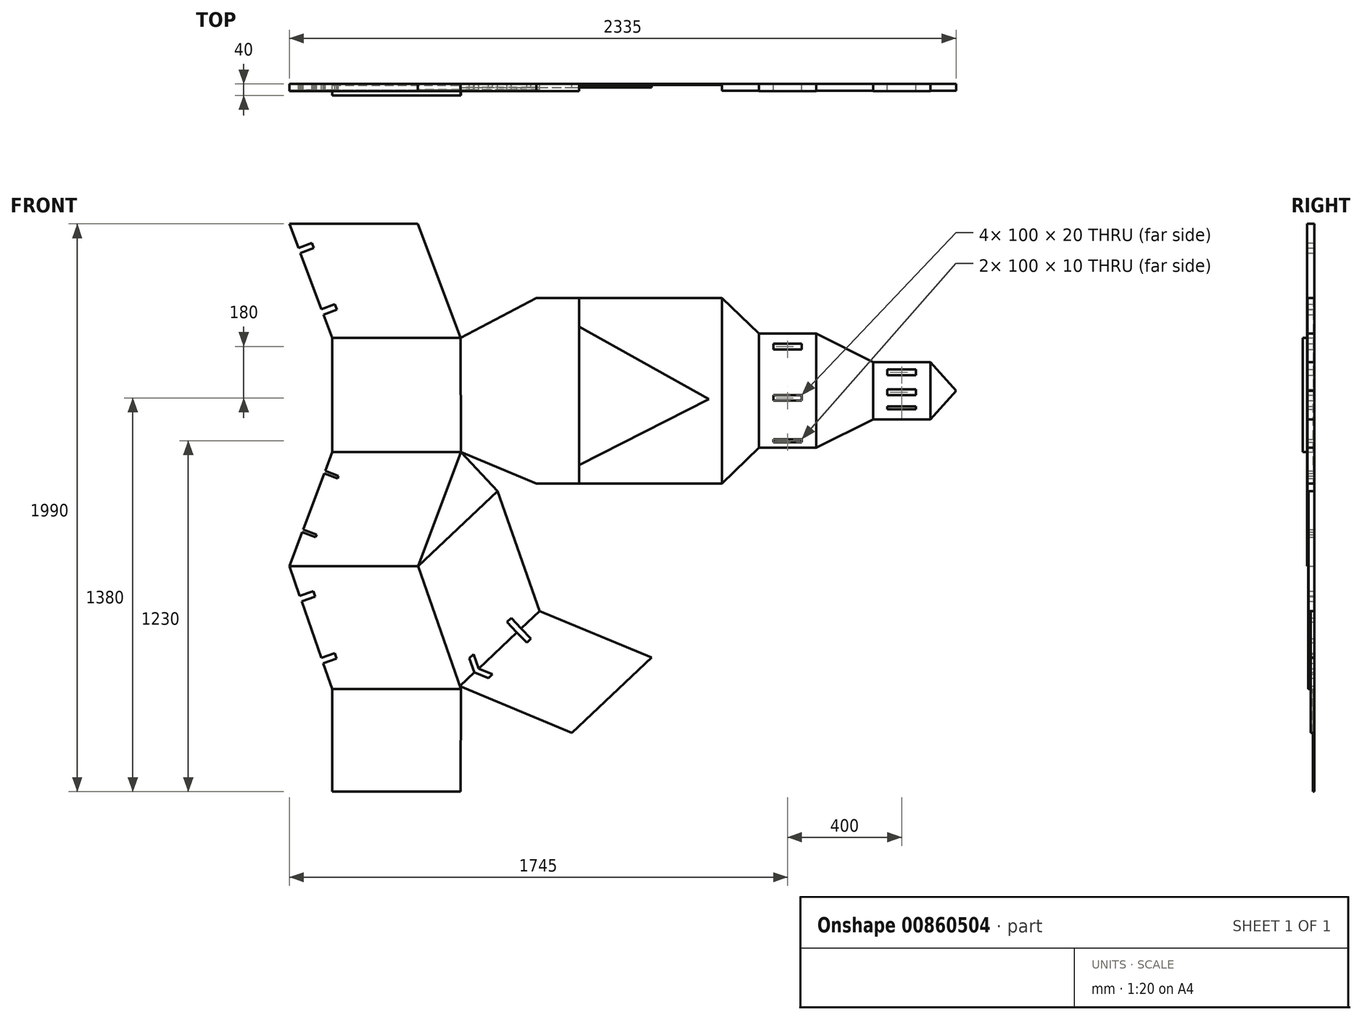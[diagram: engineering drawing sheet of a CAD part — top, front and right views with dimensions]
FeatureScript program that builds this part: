
annotation { "Feature Type Name" : "Feature", "Feature Type Description" : "" }
export const myFeature = defineFeature(function(context is Context, id is Id, definition is map)
    precondition{}
    {
        {
            var Q0;
            Q0=qCreatedBy(makeId("Front.planeOp"),FACE);
            var sketch = newSketch(context, id + "F0", { "sketchPlane" : qUnion([Q0])});
            skLineSegment(sketch, "E0", {"start": v(-600.47, 910) * mm, "end": v(-150.47, 910) * mm});
            skLineSegment(sketch, "E1", {"start": v(-150.47, 910) * mm, "end": v(-0.47, 510) * mm});
            skLineSegment(sketch, "E2", {"start": v(-0.47, 510) * mm, "end": v(-450.47, 510) * mm});
            skLineSegment(sketch, "E3", {"start": v(-450.47, 510) * mm, "end": v(-481.09, 591.65) * mm});
            skLineSegment(sketch, "E4", {"start": v(-450.47, 510) * mm, "end": v(-450.47, 110) * mm});
            skLineSegment(sketch, "E5", {"start": v(-450.47, 110) * mm, "end": v(0, 110) * mm});
            skLineSegment(sketch, "E6", {"start": v(0, 110) * mm, "end": v(-0.47, 510) * mm});
            skLineSegment(sketch, "E7", {"start": v(-450.47, 110) * mm, "end": v(-475.05, 44.46) * mm});
            skLineSegment(sketch, "E8", {"start": v(-600.47, -290) * mm, "end": v(-150, -290) * mm});
            skLineSegment(sketch, "E9", {"start": v(-150, -290) * mm, "end": v(0, 110) * mm});
            skLineSegment(sketch, "E10", {"start": v(-600.47, -290) * mm, "end": v(-564.24, -393.86) * mm});
            skLineSegment(sketch, "E11", {"start": v(-450.47, -720) * mm, "end": v(0, -720) * mm});
            skLineSegment(sketch, "E12", {"start": v(0, -720) * mm, "end": v(-150, -290) * mm});
            skLineSegment(sketch, "E13", {"start": v(-450.47, -720) * mm, "end": v(-450.47, -1080) * mm});
            skLineSegment(sketch, "E14", {"start": v(-450.47, -1080) * mm, "end": v(-0.47, -1080) * mm});
            skLineSegment(sketch, "E15", {"start": v(-0.47, -1080) * mm, "end": v(0, -720) * mm});
            skLineSegment(sketch, "E16", {"start": v(-0.47, 510) * mm, "end": v(264.53, 650) * mm});
            skLineSegment(sketch, "E17", {"start": v(264.53, 650) * mm, "end": v(414.53, 650) * mm});
            skLineSegment(sketch, "E18", {"start": v(414.53, 650) * mm, "end": v(414.53, 0) * mm});
            skLineSegment(sketch, "E19", {"start": v(414.53, 0) * mm, "end": v(264.53, 0) * mm});
            skLineSegment(sketch, "E20", {"start": v(264.53, 0) * mm, "end": v(0, 110) * mm});
            skLineSegment(sketch, "E21.bottom", {"start": v(414.53, 650) * mm, "end": v(914.53, 650) * mm});
            skLineSegment(sketch, "E21.top", {"start": v(414.53, 0) * mm, "end": v(914.53, 0) * mm});
            skLineSegment(sketch, "E21.right", {"start": v(914.53, 650) * mm, "end": v(914.53, 0) * mm});
            skPoint(sketch, "E22", {"position": v(414.53, 65) * mm});
            skPoint(sketch, "E23", {"position": v(414.53, 550) * mm});
            skPoint(sketch, "E24", {"position": v(869.53, 295) * mm});
            skLineSegment(sketch, "E25", {"start": v(414.53, 550) * mm, "end": v(869.53, 295) * mm});
            skLineSegment(sketch, "E26", {"start": v(414.53, 65) * mm, "end": v(869.53, 295) * mm});
            skLineSegment(sketch, "E27", {"start": v(914.53, 650) * mm, "end": v(1044.53, 525) * mm});
            skLineSegment(sketch, "E28", {"start": v(1044.53, 525) * mm, "end": v(1044.53, 125) * mm});
            skLineSegment(sketch, "E29", {"start": v(1044.53, 125) * mm, "end": v(914.53, 0) * mm});
            skLineSegment(sketch, "E30.bottom", {"start": v(1044.53, 525) * mm, "end": v(1244.53, 525) * mm});
            skLineSegment(sketch, "E30.top", {"start": v(1044.53, 125) * mm, "end": v(1244.53, 125) * mm});
            skLineSegment(sketch, "E30.right", {"start": v(1244.53, 525) * mm, "end": v(1244.53, 125) * mm});
            skLineSegment(sketch, "E31", {"start": v(1244.53, 525) * mm, "end": v(1444.53, 425) * mm});
            skLineSegment(sketch, "E32", {"start": v(1444.53, 425) * mm, "end": v(1444.53, 225) * mm});
            skLineSegment(sketch, "E33", {"start": v(1444.53, 225) * mm, "end": v(1244.53, 125) * mm});
            skLineSegment(sketch, "E34.bottom", {"start": v(1444.53, 425) * mm, "end": v(1644.53, 425) * mm});
            skLineSegment(sketch, "E34.top", {"start": v(1444.53, 225) * mm, "end": v(1644.53, 225) * mm});
            skLineSegment(sketch, "E34.right", {"start": v(1644.53, 425) * mm, "end": v(1644.53, 225) * mm});
            skLineSegment(sketch, "E35", {"start": v(1644.53, 225) * mm, "end": v(1734.53, 325) * mm});
            skLineSegment(sketch, "E36", {"start": v(1734.53, 325) * mm, "end": v(1644.53, 425) * mm});
            skLineSegment(sketch, "E37", {"start": v(-150, -290) * mm, "end": v(128.9, -26.38) * mm});
            skLineSegment(sketch, "E38", {"start": v(128.9, -26.38) * mm, "end": v(0, 110) * mm});
            skLineSegment(sketch, "E39", {"start": v(128.9, -26.38) * mm, "end": v(275.61, -446.93) * mm});
            skLineSegment(sketch, "E40", {"start": v(275.61, -446.93) * mm, "end": v(211.1, -507.92) * mm});
            skLineSegment(sketch, "E41", {"start": v(275.61, -446.93) * mm, "end": v(667.98, -610.25) * mm});
            skLineSegment(sketch, "E42", {"start": v(-3.3, -710.56) * mm, "end": v(389.07, -873.88) * mm});
            skLineSegment(sketch, "E43", {"start": v(389.07, -873.88) * mm, "end": v(667.98, -610.25) * mm});
            skLineSegment(sketch, "E44", {"start": v(-568.87, 825.73) * mm, "end": v(-522.05, 843.29) * mm});
            skLineSegment(sketch, "E45", {"start": v(-522.05, 843.29) * mm, "end": v(-515.03, 824.56) * mm});
            skLineSegment(sketch, "E46", {"start": v(-515.03, 824.56) * mm, "end": v(-561.84, 807) * mm});
            skLineSegment(sketch, "E47", {"start": v(-488.1, 610.37) * mm, "end": v(-441.3, 627.93) * mm});
            skLineSegment(sketch, "E48", {"start": v(-441.3, 627.93) * mm, "end": v(-434.27, 609.2) * mm});
            skLineSegment(sketch, "E49", {"start": v(-434.27, 609.2) * mm, "end": v(-481.09, 591.65) * mm});
            skLineSegment(sketch, "E50.trimOffspring", {"start": v(-568.87, 825.73) * mm, "end": v(-600.47, 910) * mm});
            skLineSegment(sketch, "E51.trimOffspring", {"start": v(-488.1, 610.37) * mm, "end": v(-561.84, 807) * mm});
            skLineSegment(sketch, "E52", {"start": v(-475.05, 44.46) * mm, "end": v(-428.23, 26.9) * mm});
            skLineSegment(sketch, "E53", {"start": v(-428.23, 26.9) * mm, "end": v(-431.74, 17.54) * mm});
            skLineSegment(sketch, "E54", {"start": v(-431.74, 17.54) * mm, "end": v(-478.56, 35.1) * mm});
            skLineSegment(sketch, "E55", {"start": v(-552.3, -161.54) * mm, "end": v(-505.48, -179.1) * mm});
            skLineSegment(sketch, "E56", {"start": v(-505.48, -179.1) * mm, "end": v(-508.99, -188.45) * mm});
            skLineSegment(sketch, "E57", {"start": v(-508.99, -188.45) * mm, "end": v(-555.8, -170.9) * mm});
            skLineSegment(sketch, "E58.trimOffspring", {"start": v(-478.56, 35.1) * mm, "end": v(-552.3, -161.54) * mm});
            skLineSegment(sketch, "E59.trimOffspring", {"start": v(-555.8, -170.9) * mm, "end": v(-600.47, -290) * mm});
            skLineSegment(sketch, "E60", {"start": v(-564.24, -393.86) * mm, "end": v(-517.03, -377.4) * mm});
            skLineSegment(sketch, "E61", {"start": v(-517.03, -377.4) * mm, "end": v(-510.44, -396.28) * mm});
            skLineSegment(sketch, "E62", {"start": v(-510.44, -396.28) * mm, "end": v(-557.65, -412.75) * mm});
            skLineSegment(sketch, "E63", {"start": v(-441.27, -594.56) * mm, "end": v(-441.27, -594.56) * mm});
            skLineSegment(sketch, "E64", {"start": v(-441.27, -594.56) * mm, "end": v(-488.48, -611.03) * mm});
            skLineSegment(sketch, "E65", {"start": v(-441.27, -594.56) * mm, "end": v(-434.68, -613.44) * mm});
            skLineSegment(sketch, "E66", {"start": v(-434.68, -613.44) * mm, "end": v(-481.9, -629.91) * mm});
            skLineSegment(sketch, "E67.trimOffspring", {"start": v(-557.65, -412.75) * mm, "end": v(-488.48, -611.03) * mm});
            skLineSegment(sketch, "E68.trimOffspring", {"start": v(-481.9, -629.91) * mm, "end": v(-450.47, -720) * mm});
            skLineSegment(sketch, "E69.bottom", {"start": v(1094.53, 490) * mm, "end": v(1194.53, 490) * mm});
            skLineSegment(sketch, "E69.top", {"start": v(1094.53, 470) * mm, "end": v(1194.53, 470) * mm});
            skLineSegment(sketch, "E69.left", {"start": v(1094.53, 490) * mm, "end": v(1094.53, 470) * mm});
            skLineSegment(sketch, "E69.right", {"start": v(1194.53, 490) * mm, "end": v(1194.53, 470) * mm});
            skLineSegment(sketch, "E70.bottom", {"start": v(1094.53, 310) * mm, "end": v(1194.53, 310) * mm});
            skLineSegment(sketch, "E70.top", {"start": v(1094.53, 290) * mm, "end": v(1194.53, 290) * mm});
            skLineSegment(sketch, "E70.left", {"start": v(1094.53, 310) * mm, "end": v(1094.53, 290) * mm});
            skLineSegment(sketch, "E70.right", {"start": v(1194.53, 310) * mm, "end": v(1194.53, 290) * mm});
            skLineSegment(sketch, "E71.bottom", {"start": v(1094.53, 155) * mm, "end": v(1194.53, 155) * mm});
            skLineSegment(sketch, "E71.top", {"start": v(1094.53, 145) * mm, "end": v(1194.53, 145) * mm});
            skLineSegment(sketch, "E71.left", {"start": v(1094.53, 155) * mm, "end": v(1094.53, 145) * mm});
            skLineSegment(sketch, "E71.right", {"start": v(1194.53, 155) * mm, "end": v(1194.53, 145) * mm});
            skLineSegment(sketch, "E72.bottom", {"start": v(1494.53, 400) * mm, "end": v(1594.53, 400) * mm});
            skLineSegment(sketch, "E72.top", {"start": v(1494.53, 380) * mm, "end": v(1594.53, 380) * mm});
            skLineSegment(sketch, "E72.left", {"start": v(1494.53, 400) * mm, "end": v(1494.53, 380) * mm});
            skLineSegment(sketch, "E72.right", {"start": v(1594.53, 400) * mm, "end": v(1594.53, 380) * mm});
            skLineSegment(sketch, "E73.bottom", {"start": v(1494.53, 330) * mm, "end": v(1594.53, 330) * mm});
            skLineSegment(sketch, "E73.top", {"start": v(1494.53, 310) * mm, "end": v(1594.53, 310) * mm});
            skLineSegment(sketch, "E73.left", {"start": v(1494.53, 330) * mm, "end": v(1494.53, 310) * mm});
            skLineSegment(sketch, "E73.right", {"start": v(1594.53, 330) * mm, "end": v(1594.53, 310) * mm});
            skLineSegment(sketch, "E74.bottom", {"start": v(1494.53, 270) * mm, "end": v(1594.53, 270) * mm});
            skLineSegment(sketch, "E74.top", {"start": v(1494.53, 260) * mm, "end": v(1594.53, 260) * mm});
            skLineSegment(sketch, "E74.left", {"start": v(1494.53, 270) * mm, "end": v(1494.53, 260) * mm});
            skLineSegment(sketch, "E74.right", {"start": v(1594.53, 270) * mm, "end": v(1594.53, 260) * mm});
            skPoint(sketch, "E75", {"position": v(47.58, -662.47) * mm});
            skPoint(sketch, "E76", {"position": v(62.11, -648.74) * mm});
            skPoint(sketch, "E77", {"position": v(196.56, -521.65) * mm});
            skPoint(sketch, "E78", {"position": v(211.1, -507.92) * mm});
            skLineSegment(sketch, "E79", {"start": v(47.58, -662.47) * mm, "end": v(30.14, -612.47) * mm});
            skLineSegment(sketch, "E80", {"start": v(30.14, -612.47) * mm, "end": v(44.67, -598.74) * mm});
            skLineSegment(sketch, "E81", {"start": v(44.67, -598.74) * mm, "end": v(62.11, -648.74) * mm});
            skLineSegment(sketch, "E82.MirrorCS", {"start": v(47.58, -662.47) * mm, "end": v(96.52, -682.7) * mm});
            skLineSegment(sketch, "E83.MirrorCS", {"start": v(111.05, -668.96) * mm, "end": v(62.11, -648.74) * mm});
            skLineSegment(sketch, "E84.MirrorCS", {"start": v(96.52, -682.7) * mm, "end": v(111.05, -668.96) * mm});
            skLineSegment(sketch, "E85.trimOffspring", {"start": v(47.58, -662.47) * mm, "end": v(-3.3, -710.56) * mm});
            skLineSegment(sketch, "E86", {"start": v(196.56, -521.65) * mm, "end": v(162.21, -485.32) * mm});
            skLineSegment(sketch, "E87", {"start": v(162.21, -485.32) * mm, "end": v(176.75, -471.58) * mm});
            skLineSegment(sketch, "E88", {"start": v(176.75, -471.58) * mm, "end": v(211.1, -507.92) * mm});
            skLineSegment(sketch, "E89.MirrorCS", {"start": v(196.56, -521.65) * mm, "end": v(230.9, -558) * mm});
            skLineSegment(sketch, "E90.MirrorCS", {"start": v(245.44, -544.25) * mm, "end": v(211.1, -507.92) * mm});
            skLineSegment(sketch, "E91.MirrorCS", {"start": v(230.9, -558) * mm, "end": v(245.44, -544.25) * mm});
            skLineSegment(sketch, "E92.trimOffspring", {"start": v(196.56, -521.65) * mm, "end": v(62.11, -648.74) * mm});
            skSolve(sketch);
        }
        {
            var Q0;
            Q0=makeQuery(id+"F0.imprint","IMPRINT",FACE,{"disambiguationData":[TD([[makeQuery(id+"F0.imprint","IMPRINT",EDGE,{"derivedFrom":sQuery(id+"F0.wireOp",EDGE,"E0")}),-1.0]])]});
            extrude(context, id + "F1", {"entities" : qUnion([Q0]), "depth" : 25 * mm, "offsetDistance" : 25 * mm});
        }
        {
            var Q0;
            Q0=makeQuery(id+"F0.imprint","IMPRINT",FACE,{"disambiguationData":[TD([[makeQuery(id+"F0.imprint","IMPRINT",EDGE,{"derivedFrom":sQuery(id+"F0.wireOp",EDGE,"E2")}),1.0]])]});
            extrude(context, id + "F2", {"entities" : qUnion([Q0]), "operationType" : NewBodyOperationType.ADD, "depth" : 40 * mm, "offsetDistance" : 25 * mm});
        }
        {
            var Q0;
            Q0=makeQuery(id+"F0.imprint","IMPRINT",FACE,{"disambiguationData":[TD([[makeQuery(id+"F0.imprint","IMPRINT",EDGE,{"derivedFrom":sQuery(id+"F0.wireOp",EDGE,"E5")}),-1.0]])]});
            extrude(context, id + "F3", {"entities" : qUnion([Q0]), "operationType" : NewBodyOperationType.ADD, "depth" : 25 * mm, "offsetDistance" : 25 * mm});
        }
        {
            var Q0;
            Q0=makeQuery(id+"F0.imprint","IMPRINT",FACE,{"disambiguationData":[TD([[makeQuery(id+"F0.imprint","IMPRINT",EDGE,{"derivedFrom":sQuery(id+"F0.wireOp",EDGE,"E8")}),-1.0]])]});
            extrude(context, id + "F4", {"entities" : qUnion([Q0]), "operationType" : NewBodyOperationType.ADD, "depth" : 21 * mm, "offsetDistance" : 25 * mm});
        }
        {
            var Q0;
            Q0=makeQuery(id+"F0.imprint","IMPRINT",FACE,{"disambiguationData":[TD([[makeQuery(id+"F0.imprint","IMPRINT",EDGE,{"derivedFrom":sQuery(id+"F0.wireOp",EDGE,"E11")}),-1.0]])]});
            extrude(context, id + "F5", {"entities" : qUnion([Q0]), "operationType" : NewBodyOperationType.ADD, "depth" : 4 * mm, "offsetDistance" : 25 * mm});
        }
        {
            var Q0;
            Q0=makeQuery(id+"F0.imprint","IMPRINT",FACE,{"disambiguationData":[TD([[makeQuery(id+"F0.imprint","IMPRINT",EDGE,{"derivedFrom":sQuery(id+"F0.wireOp",EDGE,"E6")}),-1.0]])]});
            extrude(context, id + "F6", {"entities" : qUnion([Q0]), "operationType" : NewBodyOperationType.ADD, "depth" : 25 * mm, "offsetDistance" : 25 * mm});
        }
        {
            var Q0;
            {var subQ3=sQuery(id+"F0.wireOp",EDGE,"E21.bottom");Q0=makeQuery(id+"F0.imprint","IMPRINT",FACE,{"disambiguationData":[TD([[makeQuery(id+"F0.imprint","IMPRINT",EDGE,{"derivedFrom":subQ3}),-1.0]])]});}
            extrude(context, id + "F7", {"entities" : qUnion([Q0]), "operationType" : NewBodyOperationType.ADD, "depth" : 3 * mm, "offsetDistance" : 25 * mm});
        }
        {
            var Q0;
            Q0=makeQuery(id+"F0.imprint","IMPRINT",FACE,{"disambiguationData":[TD([[makeQuery(id+"F0.imprint","IMPRINT",EDGE,{"derivedFrom":sQuery(id+"F0.wireOp",EDGE,"E21.right")}),1.0]])]});
            extrude(context, id + "F8", {"entities" : qUnion([Q0]), "operationType" : NewBodyOperationType.ADD, "depth" : 23 * mm, "offsetDistance" : 25 * mm});
        }
        {
            var Q0;
            Q0=makeQuery(id+"F0.imprint","IMPRINT",FACE,{"disambiguationData":[TD([[makeQuery(id+"F0.imprint","IMPRINT",EDGE,{"derivedFrom":sQuery(id+"F0.wireOp",EDGE,"E30.bottom")}),-1.0]])]});
            extrude(context, id + "F9", {"entities" : qUnion([Q0]), "operationType" : NewBodyOperationType.ADD, "depth" : 25 * mm, "offsetDistance" : 25 * mm});
        }
        {
            var Q0;
            Q0=makeQuery(id+"F0.imprint","IMPRINT",FACE,{"disambiguationData":[TD([[makeQuery(id+"F0.imprint","IMPRINT",EDGE,{"derivedFrom":sQuery(id+"F0.wireOp",EDGE,"E30.right")}),1.0]])]});
            extrude(context, id + "F10", {"entities" : qUnion([Q0]), "operationType" : NewBodyOperationType.ADD, "depth" : 23 * mm, "offsetDistance" : 25 * mm});
        }
        {
            var Q0;
            Q0=makeQuery(id+"F0.imprint","IMPRINT",FACE,{"disambiguationData":[TD([[makeQuery(id+"F0.imprint","IMPRINT",EDGE,{"derivedFrom":sQuery(id+"F0.wireOp",EDGE,"E34.bottom")}),-1.0]])]});
            extrude(context, id + "F11", {"entities" : qUnion([Q0]), "operationType" : NewBodyOperationType.ADD, "depth" : 25 * mm, "offsetDistance" : 25 * mm});
        }
        {
            var Q0;
            Q0=makeQuery(id+"F0.imprint","IMPRINT",FACE,{"disambiguationData":[TD([[makeQuery(id+"F0.imprint","IMPRINT",EDGE,{"derivedFrom":sQuery(id+"F0.wireOp",EDGE,"E34.right")}),1.0]])]});
            extrude(context, id + "F12", {"entities" : qUnion([Q0]), "operationType" : NewBodyOperationType.ADD, "depth" : 23 * mm, "offsetDistance" : 25 * mm});
        }
        {
            var Q0;
            Q0=makeQuery(id+"F0.imprint","IMPRINT",FACE,{"disambiguationData":[TD([[makeQuery(id+"F0.imprint","IMPRINT",EDGE,{"derivedFrom":sQuery(id+"F0.wireOp",EDGE,"E9")}),-1.0]])]});
            extrude(context, id + "F13", {"entities" : qUnion([Q0]), "operationType" : NewBodyOperationType.ADD, "depth" : 23 * mm, "offsetDistance" : 25 * mm});
        }
        {
            var Q0;
            {var subQ0=sQuery(id+"F0.wireOp",EDGE,"E37");Q0=makeQuery(id+"F0.imprint","IMPRINT",FACE,{"disambiguationData":[TD([[makeQuery(id+"F0.imprint","IMPRINT",EDGE,{"derivedFrom":subQ0}),-1.0]])]});}
            extrude(context, id + "F14", {"entities" : qUnion([Q0]), "operationType" : NewBodyOperationType.ADD, "depth" : 20 * mm, "offsetDistance" : 25 * mm});
        }
        {
            var Q0;
            Q0=makeQuery(id+"F0.imprint","IMPRINT",FACE,{"disambiguationData":[TD([[makeQuery(id+"F0.imprint","IMPRINT",EDGE,{"derivedFrom":sQuery(id+"F0.wireOp",EDGE,"E40")}),1.0]])]});
            extrude(context, id + "F15", {"entities" : qUnion([Q0]), "operationType" : NewBodyOperationType.ADD, "depth" : 12 * mm, "offsetDistance" : 25 * mm});
        }
    });
